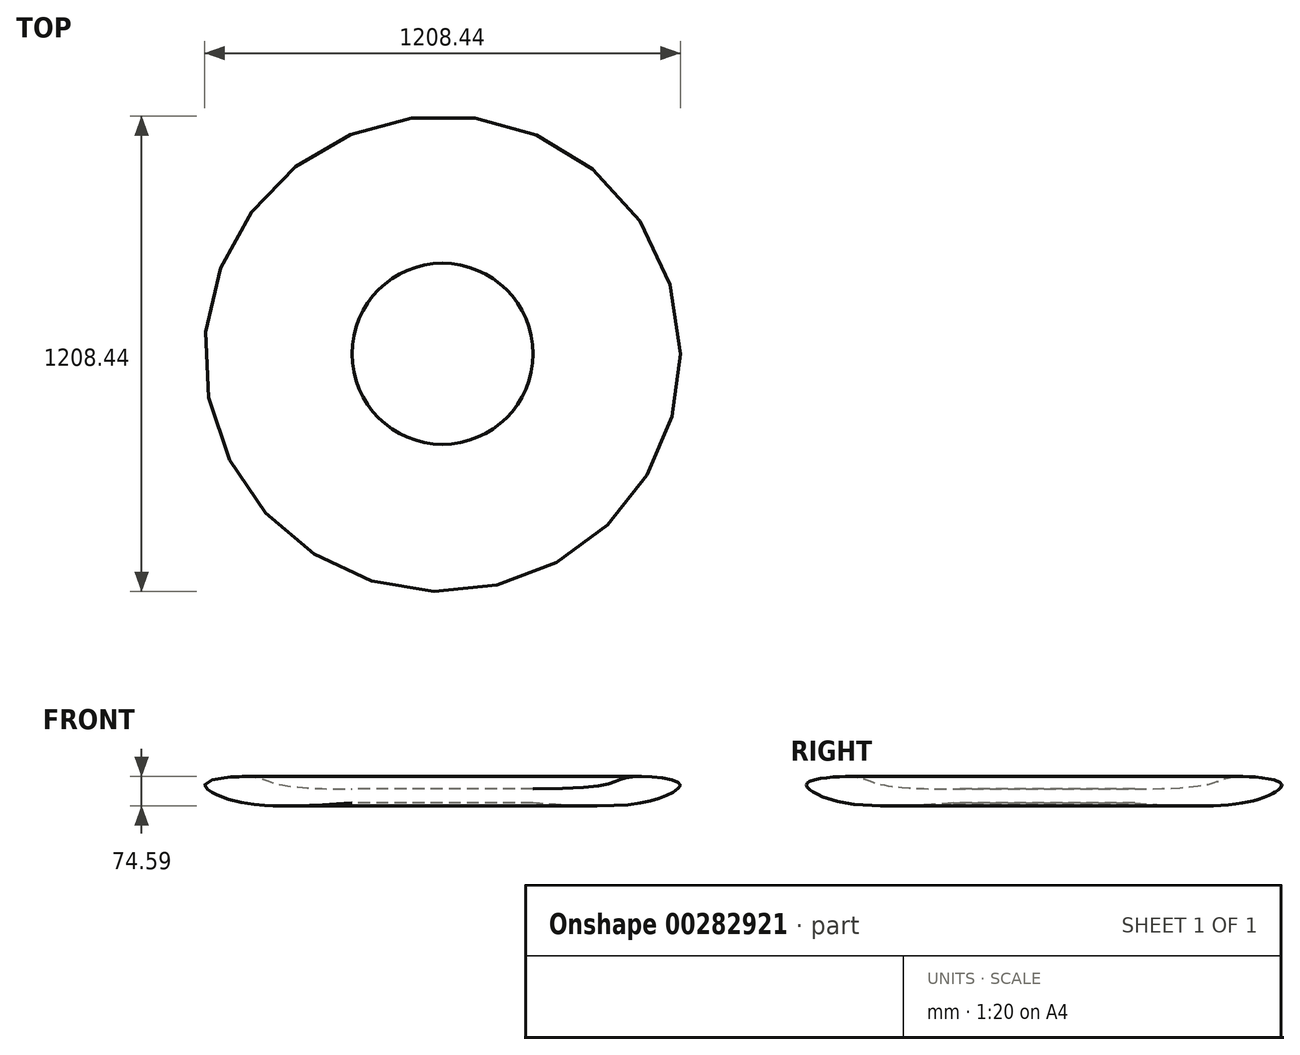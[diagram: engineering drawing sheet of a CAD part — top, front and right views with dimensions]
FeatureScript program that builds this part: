
annotation { "Feature Type Name" : "Feature", "Feature Type Description" : "" }
export const myFeature = defineFeature(function(context is Context, id is Id, definition is map)
    precondition{}
    {
        {
            var Q0;
            Q0=qCreatedBy(makeId("Front.planeOp"),FACE);
            var sketch = newSketch(context, id + "F0", { "sketchPlane" : qUnion([Q0])});
            skLineSegment(sketch, "E0", {"start": v(-230, 12.59) * mm, "end": v(-600, 12.59) * mm, "construction": true});
            skLineSegment(sketch, "E1", {"start": v(0, 0) * mm, "end": v(0, 203.05) * mm, "construction": true});
            skFitSpline(sketch, "E2", {"points": [v(-230, 12.59) * mm, v(-481.18, 43.19) * mm, v(-603, 26.3) * mm, v(-577.89, 0) * mm, v(-230, -23.07) * mm], "startDerivative": vector(-2217.53, 0) * mm, "endDerivative": vector(1796.85, 137.5) * mm});
            skSolve(sketch);
        }
        {
            var Q0;
            Q0 = qConstructionFilter(qBodyType(qCreatedBy(id + "F0" ,EDGE), BodyType.WIRE), ConstructionObject.NO);
            var Q1;
            Q1=sQuery(id+"F0.wireOp",EDGE,"E1");
            revolve(context, id + "F1", {"bodyType" : ToolBodyType.SURFACE, "surfaceEntities" : qUnion([Q0]), "axis" : qUnion([Q1]), "revolveType" : RevolveType.FULL});
        }
    });
